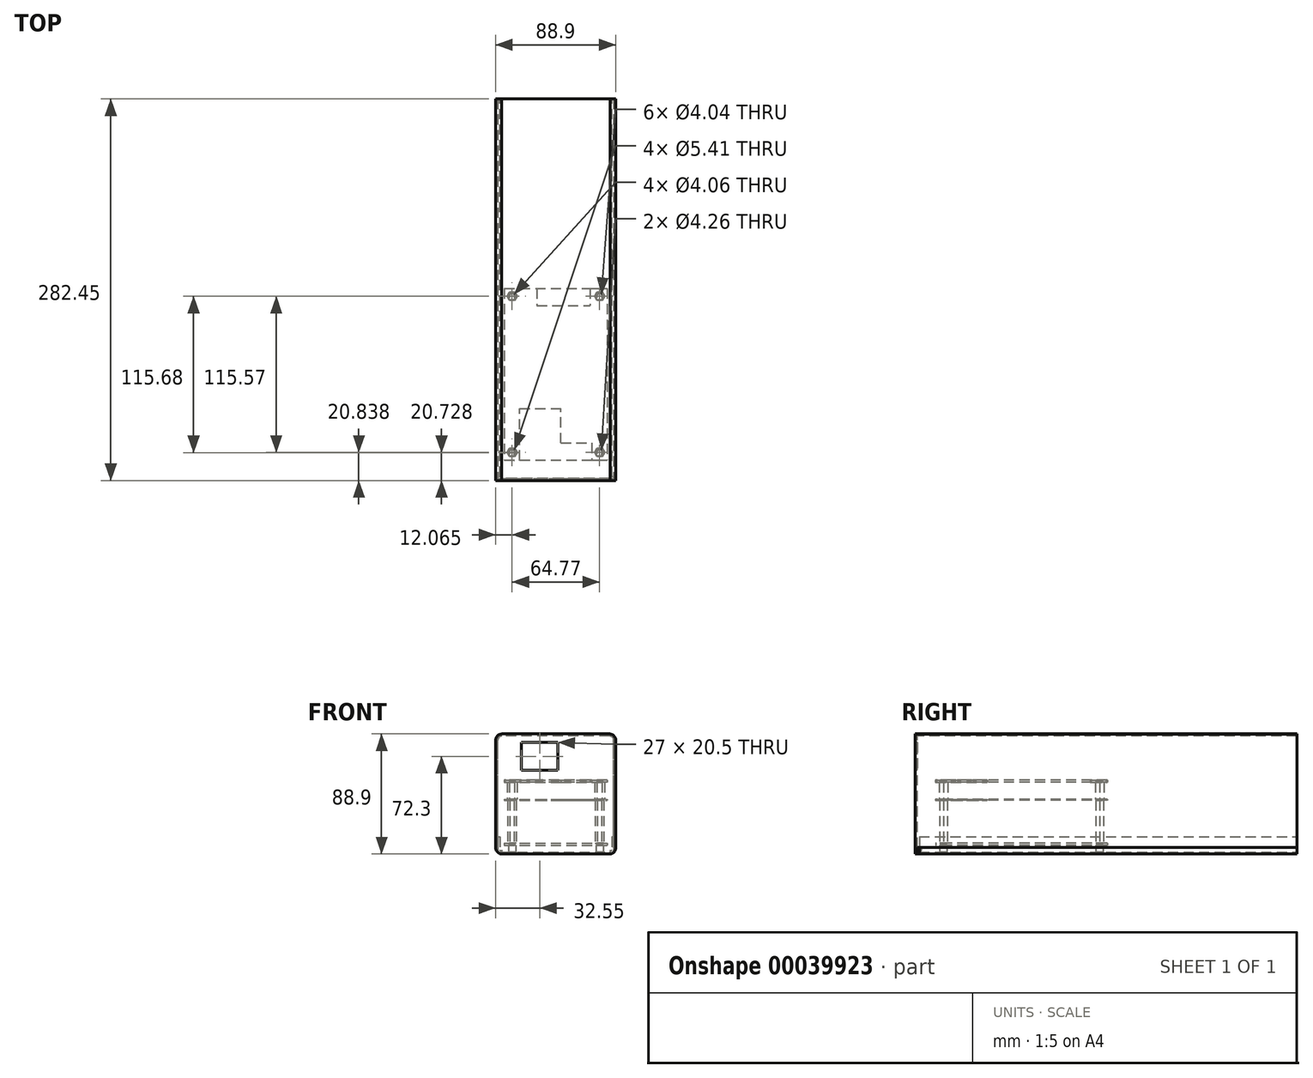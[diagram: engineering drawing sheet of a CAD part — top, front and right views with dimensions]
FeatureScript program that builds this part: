
annotation { "Feature Type Name" : "Feature", "Feature Type Description" : "" }
export const myFeature = defineFeature(function(context is Context, id is Id, definition is map)
    precondition{}
    {
        {
            var Q0;
            Q0=qCreatedBy(makeId("Front.planeOp"),FACE);
            var sketch = newSketch(context, id + "F0", { "sketchPlane" : qUnion([Q0])});
            skLineSegment(sketch, "E0.rect.top", {"start": v(-39.88, -44.45) * mm, "end": v(39.88, -44.45) * mm});
            skLineSegment(sketch, "E0.rect.left", {"start": v(-42.93, -31.75) * mm, "end": v(-42.93, -41.4) * mm});
            skLineSegment(sketch, "E0.rect.right", {"start": v(42.93, -31.75) * mm, "end": v(42.93, -41.4) * mm});
            skPoint(sketch, "E0.rect.middle", {"position": v(0, 0) * mm});
            skPoint(sketch, "E1.visualSharp", {"position": v(-42.93, 44.45) * mm});
            skPoint(sketch, "E2.visualSharp", {"position": v(42.93, 44.45) * mm});
            skPoint(sketch, "E3.visualSharp", {"position": v(42.93, -44.45) * mm});
            skArc(sketch, "E3.filletArc", {"start": v(39.88, -44.45) * mm, "mid": v(42.03, -43.56) * mm, "end": v(42.93, -41.4) * mm});
            skPoint(sketch, "E4.visualSharp", {"position": v(-42.93, -44.45) * mm});
            skArc(sketch, "E4.filletArc", {"start": v(-42.93, -41.4) * mm, "mid": v(-42.03, -43.56) * mm, "end": v(-39.88, -44.45) * mm});
            skLineSegment(sketch, "E5.3", {"start": v(41.4, -31.75) * mm, "end": v(41.4, -41.4) * mm});
            skLineSegment(sketch, "E5.4", {"start": v(-41.4, -31.75) * mm, "end": v(-41.4, -41.4) * mm});
            skLineSegment(sketch, "E6", {"start": v(-42.93, -31.75) * mm, "end": v(-41.4, -31.75) * mm});
            skLineSegment(sketch, "E7.trimOffspring", {"start": v(41.4, -31.75) * mm, "end": v(42.93, -31.75) * mm});
            skArc(sketch, "E8.0", {"start": v(39.88, -42.93) * mm, "mid": v(40.96, -42.48) * mm, "end": v(41.4, -41.4) * mm});
            skLineSegment(sketch, "E8.1", {"start": v(-39.88, -42.93) * mm, "end": v(39.88, -42.93) * mm});
            skArc(sketch, "E8.2", {"start": v(-41.4, -41.4) * mm, "mid": v(-40.96, -42.48) * mm, "end": v(-39.88, -42.93) * mm});
            skSolve(sketch);
        }
        {
            var Q0;
            Q0 = qSketchRegion(id + "F0", true);
            var Q1;
            Q1 = qConstructionFilter(qBodyType(qCreatedBy(id + "F0" ,EDGE), BodyType.WIRE), ConstructionObject.NO);
            extrude(context, id + "F1", {"entities" : qUnion([Q0]), "surfaceEntities" : qUnion([Q1]), "depth" : 152.4 * mm, "hasSecondDirection" : true, "secondDirectionOppositeDirection" : true, "secondDirectionDepth" : 127 * mm});
        }
        {
            var Q0;
            Q0=makeQuery(id+"F1.opExtrude","SWEPT_FACE",FACE,{"disambiguationData":[OSD([sQuery(id+"F0.wireOp",EDGE,"E8.1")])]});
            var sketch = newSketch(context, id + "F2", { "sketchPlane" : qUnion([Q0])});
            skLineSegment(sketch, "E9.rect.bottom", {"start": v(32.39, -19.04) * mm, "end": v(-32.39, -19.04) * mm, "construction": true});
            skLineSegment(sketch, "E9.rect.top", {"start": v(32.38, -134.61) * mm, "end": v(-32.39, -134.61) * mm, "construction": true});
            skLineSegment(sketch, "E9.rect.left", {"start": v(32.39, -19.04) * mm, "end": v(32.38, -134.61) * mm, "construction": true});
            skLineSegment(sketch, "E9.rect.right", {"start": v(-32.39, -19.04) * mm, "end": v(-32.39, -134.61) * mm, "construction": true});
            skPoint(sketch, "E9.rect.middle", {"position": v(0, -76.83) * mm});
            skCircle(sketch, "E10", {"center": v(-32.39, -19.04) * mm, "radius": 2.7 * mm});
            skCircle(sketch, "E11", {"center": v(32.39, -19.04) * mm, "radius": 2.7 * mm});
            skCircle(sketch, "E12", {"center": v(-32.39, -134.61) * mm, "radius": 2.7 * mm});
            skCircle(sketch, "E13", {"center": v(32.38, -134.61) * mm, "radius": 2.7 * mm});
            skSolve(sketch);
        }
        {
            var Q0;
            Q0 = qSketchRegion(id + "F2", true);
            extrude(context, id + "F3", {"entities" : qUnion([Q0]), "operationType" : NewBodyOperationType.REMOVE, "endBound" : BoundingType.THROUGH_ALL, "oppositeDirection" : true, "depth" : 25.4 * mm});
        }
        {
            var Q0;
            Q0=makeQuery(id+"F1.opExtrude","SWEPT_FACE",FACE,{"disambiguationData":[OSD([sQuery(id+"F0.wireOp",EDGE,"E8.1")])]});
            var sketch = newSketch(context, id + "F4", { "sketchPlane" : qUnion([Q0])});
            skCircle(sketch, "E14", {"center": v(-32.39, -19.04) * mm, "radius": 2.7 * mm});
            skCircle(sketch, "E15", {"center": v(32.39, -19.04) * mm, "radius": 2.7 * mm});
            skCircle(sketch, "E16", {"center": v(-32.39, -134.61) * mm, "radius": 2.7 * mm});
            skCircle(sketch, "E17", {"center": v(32.38, -134.61) * mm, "radius": 2.7 * mm});
            skSolve(sketch);
        }
        {
            var Q0;
            Q0 = qSketchRegion(id + "F4", true);
            extrude(context, id + "F5", {"entities" : qUnion([Q0]), "depth" : 4.83 * mm});
        }
        {
            var Q0;
            Q0=makeQuery(id+"F5.opExtrude","CAP_FACE",FACE,{"disambiguationData":[OSD([sQuery(id+"F4.wireOp",EDGE,"E14")])],"isStart":false});
            var sketch = newSketch(context, id + "F6", { "sketchPlane" : qUnion([Q0])});
            skLineSegment(sketch, "E18.rect.bottom", {"start": v(-38.1, -13.33) * mm, "end": v(38.1, -13.33) * mm});
            skLineSegment(sketch, "E18.rect.top", {"start": v(-38.1, -140.33) * mm, "end": v(38.1, -140.33) * mm});
            skLineSegment(sketch, "E18.rect.left", {"start": v(-38.1, -13.33) * mm, "end": v(-38.1, -140.33) * mm});
            skLineSegment(sketch, "E18.rect.right", {"start": v(38.1, -13.33) * mm, "end": v(38.1, -140.33) * mm});
            skPoint(sketch, "E18.rect.middle", {"position": v(0, -76.83) * mm});
            skLineSegment(sketch, "E19.rect.bottom", {"start": v(-32.39, -19.04) * mm, "end": v(32.39, -19.04) * mm, "construction": true});
            skLineSegment(sketch, "E19.rect.top", {"start": v(-32.39, -134.61) * mm, "end": v(32.39, -134.61) * mm, "construction": true});
            skLineSegment(sketch, "E19.rect.left", {"start": v(-32.39, -19.04) * mm, "end": v(-32.39, -134.61) * mm, "construction": true});
            skLineSegment(sketch, "E19.rect.right", {"start": v(32.39, -19.04) * mm, "end": v(32.39, -134.61) * mm, "construction": true});
            skCircle(sketch, "E20", {"center": v(-32.39, -19.04) * mm, "radius": 2.02 * mm});
            skCircle(sketch, "E21", {"center": v(32.39, -19.04) * mm, "radius": 2.02 * mm});
            skCircle(sketch, "E22", {"center": v(32.39, -134.61) * mm, "radius": 2.02 * mm});
            skCircle(sketch, "E23", {"center": v(-32.39, -134.61) * mm, "radius": 2.02 * mm});
            skSolve(sketch);
        }
        {
            var Q0;
            Q0 = qSketchRegion(id + "F6", true);
            extrude(context, id + "F7", {"entities" : qUnion([Q0]), "depth" : 1.6 * mm});
        }
        {
            var Q0;
            Q0=makeQuery(id+"F7.opExtrude","CAP_FACE",FACE,{"disambiguationData":[OSD([sQuery(id+"F6.wireOp",EDGE,"E18.rect.bottom"),sQuery(id+"F6.wireOp",EDGE,"E18.rect.top"),sQuery(id+"F6.wireOp",EDGE,"E18.rect.left"),sQuery(id+"F6.wireOp",EDGE,"E18.rect.right"),sQuery(id+"F6.wireOp",EDGE,"15a53e75-c34d-44fe-b530-c52fe133d88d.1"),sQuery(id+"F6.wireOp",EDGE,"E20"),sQuery(id+"F6.wireOp",EDGE,"E22"),sQuery(id+"F6.wireOp",EDGE,"E23")])],"isStart":false});
            var sketch = newSketch(context, id + "F8", { "sketchPlane" : qUnion([Q0])});
            skCircle(sketch, "E24.cCircle", {"center": v(-32.39, -19.04) * mm, "radius": 3.18 * mm, "construction": true});
            skLineSegment(sketch, "E24.0", {"start": v(-29.21, -19.04) * mm, "end": v(-30.8, -21.8) * mm});
            skLineSegment(sketch, "E24.1", {"start": v(-30.8, -21.8) * mm, "end": v(-33.97, -21.8) * mm});
            skLineSegment(sketch, "E24.2", {"start": v(-33.97, -21.8) * mm, "end": v(-35.56, -19.04) * mm});
            skLineSegment(sketch, "E24.3", {"start": v(-35.56, -19.04) * mm, "end": v(-33.97, -16.3) * mm});
            skLineSegment(sketch, "E24.4", {"start": v(-33.97, -16.3) * mm, "end": v(-30.8, -16.3) * mm});
            skLineSegment(sketch, "E24.5", {"start": v(-30.8, -16.3) * mm, "end": v(-29.21, -19.04) * mm});
            skCircle(sketch, "E25.cCircle", {"center": v(32.39, -19.04) * mm, "radius": 3.18 * mm, "construction": true});
            skLineSegment(sketch, "E25.0", {"start": v(29.21, -19.04) * mm, "end": v(30.8, -16.3) * mm});
            skLineSegment(sketch, "E25.1", {"start": v(30.8, -16.3) * mm, "end": v(33.97, -16.3) * mm});
            skLineSegment(sketch, "E25.2", {"start": v(33.97, -16.3) * mm, "end": v(35.56, -19.04) * mm});
            skLineSegment(sketch, "E25.3", {"start": v(35.56, -19.04) * mm, "end": v(33.97, -21.8) * mm});
            skLineSegment(sketch, "E25.4", {"start": v(33.97, -21.8) * mm, "end": v(30.8, -21.8) * mm});
            skLineSegment(sketch, "E25.5", {"start": v(30.8, -21.8) * mm, "end": v(29.21, -19.04) * mm});
            skCircle(sketch, "E26.cCircle", {"center": v(-32.39, -134.61) * mm, "radius": 3.18 * mm, "construction": true});
            skLineSegment(sketch, "E26.0", {"start": v(-29.2, -134.61) * mm, "end": v(-30.8, -137.36) * mm});
            skLineSegment(sketch, "E26.1", {"start": v(-30.8, -137.36) * mm, "end": v(-33.97, -137.36) * mm});
            skLineSegment(sketch, "E26.2", {"start": v(-33.97, -137.36) * mm, "end": v(-35.56, -134.61) * mm});
            skLineSegment(sketch, "E26.3", {"start": v(-35.56, -134.61) * mm, "end": v(-33.97, -131.86) * mm});
            skLineSegment(sketch, "E26.4", {"start": v(-33.97, -131.86) * mm, "end": v(-30.8, -131.86) * mm});
            skLineSegment(sketch, "E26.5", {"start": v(-30.8, -131.86) * mm, "end": v(-29.21, -134.61) * mm});
            skCircle(sketch, "E27.cCircle", {"center": v(32.39, -134.61) * mm, "radius": 3.18 * mm, "construction": true});
            skLineSegment(sketch, "E27.0", {"start": v(29.21, -134.61) * mm, "end": v(30.8, -131.86) * mm});
            skLineSegment(sketch, "E27.1", {"start": v(30.8, -131.86) * mm, "end": v(33.97, -131.86) * mm});
            skLineSegment(sketch, "E27.2", {"start": v(33.97, -131.86) * mm, "end": v(35.56, -134.61) * mm});
            skLineSegment(sketch, "E27.3", {"start": v(35.56, -134.61) * mm, "end": v(33.97, -137.36) * mm});
            skLineSegment(sketch, "E27.4", {"start": v(33.97, -137.36) * mm, "end": v(30.8, -137.36) * mm});
            skLineSegment(sketch, "E27.5", {"start": v(30.8, -137.36) * mm, "end": v(29.21, -134.61) * mm});
            skSolve(sketch);
        }
        {
            var Q0;
            Q0 = qSketchRegion(id + "F8", true);
            extrude(context, id + "F9", {"entities" : qUnion([Q0]), "depth" : 31.75 * mm});
        }
        {
            var Q0;
            Q0=makeQuery(id+"F9.opExtrude","CAP_FACE",FACE,{"disambiguationData":[OSD([sQuery(id+"F8.wireOp",EDGE,"E26.0"),sQuery(id+"F8.wireOp",EDGE,"E26.1"),sQuery(id+"F8.wireOp",EDGE,"E26.2"),sQuery(id+"F8.wireOp",EDGE,"E26.3"),sQuery(id+"F8.wireOp",EDGE,"E26.4"),sQuery(id+"F8.wireOp",EDGE,"E26.5")])],"isStart":false});
            var sketch = newSketch(context, id + "F10", { "sketchPlane" : qUnion([Q0])});
            skLineSegment(sketch, "E28.rect.bottom", {"start": v(-38.1, -13.33) * mm, "end": v(-13.97, -13.33) * mm});
            skLineSegment(sketch, "E28.rect.left", {"start": v(-38.1, -13.33) * mm, "end": v(-38.1, -102.23) * mm});
            skLineSegment(sketch, "E28.rect.right", {"start": v(38.1, -13.33) * mm, "end": v(38.1, -140.33) * mm});
            skPoint(sketch, "E28.rect.middle", {"position": v(0, -76.83) * mm});
            skCircle(sketch, "E29.0", {"center": v(-32.39, -19.04) * mm, "radius": 2.7 * mm, "construction": true});
            skCircle(sketch, "E29.1", {"center": v(32.39, -19.04) * mm, "radius": 2.7 * mm, "construction": true});
            skCircle(sketch, "E29.2", {"center": v(32.39, -134.61) * mm, "radius": 2.7 * mm, "construction": true});
            skCircle(sketch, "E29.3", {"center": v(-32.39, -134.61) * mm, "radius": 2.7 * mm, "construction": true});
            skCircle(sketch, "E30", {"center": v(-32.39, -19.04) * mm, "radius": 2.02 * mm});
            skCircle(sketch, "E31", {"center": v(32.39, -19.04) * mm, "radius": 2.02 * mm});
            skCircle(sketch, "E32", {"center": v(32.39, -134.61) * mm, "radius": 2.13 * mm});
            skLineSegment(sketch, "E33.top", {"start": v(-13.97, -26.03) * mm, "end": v(25.4, -26.03) * mm});
            skLineSegment(sketch, "E33.left", {"start": v(-13.97, -13.33) * mm, "end": v(-13.97, -26.03) * mm});
            skLineSegment(sketch, "E33.right", {"start": v(25.4, -13.33) * mm, "end": v(25.4, -26.03) * mm});
            skLineSegment(sketch, "E34.top", {"start": v(-26.67, -102.23) * mm, "end": v(3.8, -102.23) * mm});
            skLineSegment(sketch, "E34.right", {"start": v(3.81, -127.63) * mm, "end": v(3.8, -102.23) * mm});
            skLineSegment(sketch, "E35.bottom", {"start": v(3.81, -127.63) * mm, "end": v(26.67, -127.63) * mm});
            skLineSegment(sketch, "E35.right", {"start": v(26.67, -127.63) * mm, "end": v(26.67, -140.33) * mm});
            skPoint(sketch, "E36.orphan", {"position": v(-38.1, -140.33) * mm});
            skLineSegment(sketch, "E37", {"start": v(26.67, -140.33) * mm, "end": v(38.1, -140.33) * mm});
            skLineSegment(sketch, "E38.trimOffspring", {"start": v(25.4, -13.33) * mm, "end": v(38.1, -13.33) * mm});
            skLineSegment(sketch, "E39", {"start": v(-38.1, -102.23) * mm, "end": v(-38.1, -140.33) * mm});
            skLineSegment(sketch, "E40", {"start": v(-26.67, -140.55) * mm, "end": v(-26.67, -102.23) * mm});
            skLineSegment(sketch, "E41", {"start": v(-38.1, -140.33) * mm, "end": v(-26.67, -140.55) * mm});
            skCircle(sketch, "E42", {"center": v(-32.39, -134.61) * mm, "radius": 2.13 * mm});
            skSolve(sketch);
        }
        {
            var Q0;
            Q0 = qSketchRegion(id + "F10", true);
            extrude(context, id + "F11", {"entities" : qUnion([Q0]), "depth" : 0.74 * mm});
        }
        {
            var Q0;
            Q0=qCreatedBy(makeId("Right.planeOp"),FACE);
            var Q1;
            Q1=makeQuery(id+"F1.opExtrude","CAP_VERTEX",VERTEX,{"disambiguationData":[OSD([sQuery(id+"F0.wireOp",EDGE,"E8.1"),sQuery(id+"F0.wireOp",EDGE,"E8.2")])],"isStart":false});
            cPlane(context, id + "F12", {"entities" : qUnion([Q0, Q1]), "cplaneType" : CPlaneType.PLANE_POINT, "offset" : 152.4 * mm, "width" : 152.4 * mm, "height" : 152.4 * mm});
        }
        {
            var Q0;
            Q0=qCreatedBy(id+"F12.planeOp",FACE);
            var sketch = newSketch(context, id + "F13", { "sketchPlane" : qUnion([Q0])});
            skLineSegment(sketch, "E43", {"start": v(-153.92, -41.4) * mm, "end": v(-153.92, 44.45) * mm});
            skPoint(sketch, "E44.visualSharp", {"position": v(-153.92, -42.93) * mm});
            skArc(sketch, "E44.filletArc", {"start": v(-153.92, -41.4) * mm, "mid": v(-153.48, -42.48) * mm, "end": v(-152.4, -42.93) * mm});
            skLineSegment(sketch, "E45.0", {"start": v(-155.45, -41.4) * mm, "end": v(-155.45, 44.45) * mm});
            skArc(sketch, "E45.1", {"start": v(-155.45, -41.4) * mm, "mid": v(-154.56, -43.56) * mm, "end": v(-152.4, -44.45) * mm});
            skLineSegment(sketch, "E46", {"start": v(-153.92, 44.45) * mm, "end": v(-155.45, 44.45) * mm});
            skLineSegment(sketch, "E47", {"start": v(-152.4, -44.45) * mm, "end": v(-152.4, -42.93) * mm});
            skSolve(sketch);
        }
        {
            var Q0;
            Q0 = qSketchRegion(id + "F13", true);
            extrude(context, id + "F14", {"entities" : qUnion([Q0]), "operationType" : NewBodyOperationType.ADD, "depth" : 80.26 * mm});
        }
        {
            var Q0;
            Q0=makeQuery(id+"F14.opExtrude","SWEPT_FACE",FACE,{"disambiguationData":[OSD([sQuery(id+"F13.wireOp",EDGE,"E45.0")])]});
            var sketch = newSketch(context, id + "F15", { "sketchPlane" : qUnion([Q0])});
            skLineSegment(sketch, "E48.rect.bottom", {"start": v(-39.69, 44.45) * mm, "end": v(39.69, 44.45) * mm});
            skLineSegment(sketch, "E48.rect.top", {"start": v(-39.69, -44.45) * mm, "end": v(39.69, -44.45) * mm});
            skLineSegment(sketch, "E48.rect.left", {"start": v(-44.45, 39.69) * mm, "end": v(-44.45, -39.69) * mm});
            skLineSegment(sketch, "E48.rect.right", {"start": v(44.45, 39.69) * mm, "end": v(44.45, -39.69) * mm});
            skPoint(sketch, "E48.rect.middle", {"position": v(0, 0) * mm});
            skPoint(sketch, "E49.visualSharp", {"position": v(-44.45, 44.45) * mm});
            skArc(sketch, "E49.filletArc", {"start": v(-39.69, 44.45) * mm, "mid": v(-43.06, 43.06) * mm, "end": v(-44.45, 39.69) * mm});
            skPoint(sketch, "E50.visualSharp", {"position": v(44.45, 44.45) * mm});
            skArc(sketch, "E50.filletArc", {"start": v(44.45, 39.69) * mm, "mid": v(43.06, 43.06) * mm, "end": v(39.69, 44.45) * mm});
            skPoint(sketch, "E51.visualSharp", {"position": v(44.45, -44.45) * mm});
            skArc(sketch, "E51.filletArc", {"start": v(39.69, -44.45) * mm, "mid": v(43.06, -43.06) * mm, "end": v(44.45, -39.69) * mm});
            skPoint(sketch, "E52.visualSharp", {"position": v(-44.45, -44.45) * mm});
            skArc(sketch, "E52.filletArc", {"start": v(-44.45, -39.69) * mm, "mid": v(-43.06, -43.06) * mm, "end": v(-39.69, -44.45) * mm});
            skSolve(sketch);
        }
        {
            var Q0;
            Q0 = qSketchRegion(id + "F15", true);
            extrude(context, id + "F16", {"entities" : qUnion([Q0]), "operationType" : NewBodyOperationType.ADD, "oppositeDirection" : true, "depth" : 1.52 * mm});
        }
        {
            var Q0;
            Q0=makeQuery(id+"F16.boolean.opBoolean","MERGE",FACE,{"derivedFrom":[makeQuery(id+"F14.opExtrude","SWEPT_FACE",FACE,{"disambiguationData":[OSD([sQuery(id+"F13.wireOp",EDGE,"E45.0")])]}),makeQuery(id+"F16.opExtrude","CAP_FACE",FACE,{"disambiguationData":[OSD([sQuery(id+"F15.wireOp",EDGE,"E48.rect.bottom"),sQuery(id+"F15.wireOp",EDGE,"E48.rect.top"),sQuery(id+"F15.wireOp",EDGE,"E48.rect.left"),sQuery(id+"F15.wireOp",EDGE,"E48.rect.right"),sQuery(id+"F15.wireOp",EDGE,"E49.filletArc"),sQuery(id+"F15.wireOp",EDGE,"E50.filletArc"),sQuery(id+"F15.wireOp",EDGE,"E51.filletArc"),sQuery(id+"F15.wireOp",EDGE,"E52.filletArc")])],"isStart":true})]});
            var sketch = newSketch(context, id + "F17", { "sketchPlane" : qUnion([Q0])});
            skLineSegment(sketch, "E53.rect.bottom", {"start": v(-25.4, 38.1) * mm, "end": v(1.6, 38.1) * mm});
            skLineSegment(sketch, "E53.rect.top", {"start": v(-25.4, 17.6) * mm, "end": v(1.6, 17.6) * mm});
            skLineSegment(sketch, "E53.rect.left", {"start": v(-25.4, 38.1) * mm, "end": v(-25.4, 17.6) * mm});
            skLineSegment(sketch, "E53.rect.right", {"start": v(1.6, 38.1) * mm, "end": v(1.6, 17.6) * mm});
            skPoint(sketch, "E53.rect.middle", {"position": v(-11.9, 27.85) * mm});
            skSolve(sketch);
        }
        {
            var Q0;
            Q0 = qSketchRegion(id + "F17", true);
            extrude(context, id + "F18", {"entities" : qUnion([Q0]), "operationType" : NewBodyOperationType.REMOVE, "oppositeDirection" : true, "depth" : 25.4 * mm});
        }
        {
            var Q0;
            Q0=makeQuery(id+"F11.opExtrude","CAP_FACE",FACE,{"disambiguationData":[OSD([sQuery(id+"F10.wireOp",EDGE,"E28.rect.bottom"),sQuery(id+"F10.wireOp",EDGE,"E28.rect.left"),sQuery(id+"F10.wireOp",EDGE,"E28.rect.right"),sQuery(id+"F10.wireOp",EDGE,"E30"),sQuery(id+"F10.wireOp",EDGE,"E31"),sQuery(id+"F10.wireOp",EDGE,"E32"),sQuery(id+"F10.wireOp",EDGE,"E33.top"),sQuery(id+"F10.wireOp",EDGE,"E33.left"),sQuery(id+"F10.wireOp",EDGE,"E33.right"),sQuery(id+"F10.wireOp",EDGE,"E34.top"),sQuery(id+"F10.wireOp",EDGE,"E34.right"),sQuery(id+"F10.wireOp",EDGE,"E35.bottom"),sQuery(id+"F10.wireOp",EDGE,"E35.right"),sQuery(id+"F10.wireOp",EDGE,"E37"),sQuery(id+"F10.wireOp",EDGE,"E38.trimOffspring"),sQuery(id+"F10.wireOp",EDGE,"E39"),sQuery(id+"F10.wireOp",EDGE,"E40"),sQuery(id+"F10.wireOp",EDGE,"E41"),sQuery(id+"F10.wireOp",EDGE,"E42")])],"isStart":false});
            var sketch = newSketch(context, id + "F19", { "sketchPlane" : qUnion([Q0])});
            skCircle(sketch, "E54.cCircle", {"center": v(-32.39, -19.04) * mm, "radius": 3.67 * mm, "construction": true});
            skLineSegment(sketch, "E54.0", {"start": v(-28.72, -19.04) * mm, "end": v(-30.55, -22.22) * mm});
            skLineSegment(sketch, "E54.1", {"start": v(-30.55, -22.22) * mm, "end": v(-34.22, -22.22) * mm});
            skLineSegment(sketch, "E54.2", {"start": v(-34.22, -22.22) * mm, "end": v(-36.05, -19.04) * mm});
            skLineSegment(sketch, "E54.3", {"start": v(-36.05, -19.04) * mm, "end": v(-34.22, -15.87) * mm});
            skLineSegment(sketch, "E54.4", {"start": v(-34.22, -15.87) * mm, "end": v(-30.55, -15.87) * mm});
            skLineSegment(sketch, "E54.5", {"start": v(-30.55, -15.87) * mm, "end": v(-28.72, -19.04) * mm});
            skCircle(sketch, "E55.cCircle", {"center": v(32.39, -19.04) * mm, "radius": 3.67 * mm, "construction": true});
            skLineSegment(sketch, "E55.0", {"start": v(28.72, -19.04) * mm, "end": v(30.55, -15.87) * mm});
            skLineSegment(sketch, "E55.1", {"start": v(30.55, -15.87) * mm, "end": v(34.22, -15.87) * mm});
            skLineSegment(sketch, "E55.2", {"start": v(34.22, -15.87) * mm, "end": v(36.05, -19.04) * mm});
            skLineSegment(sketch, "E55.3", {"start": v(36.05, -19.04) * mm, "end": v(34.22, -22.22) * mm});
            skLineSegment(sketch, "E55.4", {"start": v(34.22, -22.22) * mm, "end": v(30.55, -22.22) * mm});
            skLineSegment(sketch, "E55.5", {"start": v(30.55, -22.22) * mm, "end": v(28.72, -19.04) * mm});
            skCircle(sketch, "E56.cCircle", {"center": v(-32.39, -134.61) * mm, "radius": 3.67 * mm, "construction": true});
            skLineSegment(sketch, "E56.0", {"start": v(-28.72, -134.61) * mm, "end": v(-30.55, -137.79) * mm});
            skLineSegment(sketch, "E56.1", {"start": v(-30.55, -137.79) * mm, "end": v(-34.22, -137.79) * mm});
            skLineSegment(sketch, "E56.2", {"start": v(-34.22, -137.79) * mm, "end": v(-36.05, -134.61) * mm});
            skLineSegment(sketch, "E56.3", {"start": v(-36.05, -134.61) * mm, "end": v(-34.22, -131.44) * mm});
            skLineSegment(sketch, "E56.4", {"start": v(-34.22, -131.44) * mm, "end": v(-30.55, -131.44) * mm});
            skLineSegment(sketch, "E56.5", {"start": v(-30.55, -131.44) * mm, "end": v(-28.72, -134.61) * mm});
            skCircle(sketch, "E57.cCircle", {"center": v(32.39, -134.61) * mm, "radius": 3.67 * mm, "construction": true});
            skLineSegment(sketch, "E57.0", {"start": v(28.72, -134.61) * mm, "end": v(30.55, -131.44) * mm});
            skLineSegment(sketch, "E57.1", {"start": v(30.55, -131.44) * mm, "end": v(34.22, -131.44) * mm});
            skLineSegment(sketch, "E57.2", {"start": v(34.22, -131.44) * mm, "end": v(36.05, -134.61) * mm});
            skLineSegment(sketch, "E57.3", {"start": v(36.05, -134.61) * mm, "end": v(34.22, -137.79) * mm});
            skLineSegment(sketch, "E57.4", {"start": v(34.22, -137.79) * mm, "end": v(30.55, -137.79) * mm});
            skLineSegment(sketch, "E57.5", {"start": v(30.55, -137.79) * mm, "end": v(28.72, -134.61) * mm});
            skSolve(sketch);
        }
        {
            var Q0;
            Q0 = qSketchRegion(id + "F19", true);
            extrude(context, id + "F20", {"entities" : qUnion([Q0]), "depth" : 12.7 * mm});
        }
        {
            var Q0;
            Q0=makeQuery(id+"F20.opExtrude","CAP_FACE",FACE,{"disambiguationData":[OSD([sQuery(id+"F19.wireOp",EDGE,"E55.0"),sQuery(id+"F19.wireOp",EDGE,"E55.1"),sQuery(id+"F19.wireOp",EDGE,"E55.2"),sQuery(id+"F19.wireOp",EDGE,"E55.3"),sQuery(id+"F19.wireOp",EDGE,"E55.4"),sQuery(id+"F19.wireOp",EDGE,"E55.5")])],"isStart":false});
            var sketch = newSketch(context, id + "F21", { "sketchPlane" : qUnion([Q0])});
            skLineSegment(sketch, "E58.0.0", {"start": v(-13.97, -13.33) * mm, "end": v(-38.1, -13.33) * mm});
            skLineSegment(sketch, "E58.0.1", {"start": v(-38.1, -13.33) * mm, "end": v(-38.1, -140.33) * mm});
            skLineSegment(sketch, "E58.0.2", {"start": v(-38.1, -140.33) * mm, "end": v(-26.67, -140.55) * mm});
            skLineSegment(sketch, "E58.0.3", {"start": v(-26.67, -140.55) * mm, "end": v(-26.67, -102.23) * mm});
            skLineSegment(sketch, "E58.0.4", {"start": v(-26.67, -102.23) * mm, "end": v(3.8, -102.23) * mm});
            skLineSegment(sketch, "E58.0.5", {"start": v(3.8, -102.23) * mm, "end": v(3.81, -127.63) * mm});
            skLineSegment(sketch, "E58.0.6", {"start": v(3.81, -127.63) * mm, "end": v(26.67, -127.63) * mm});
            skLineSegment(sketch, "E58.0.7", {"start": v(26.67, -127.63) * mm, "end": v(26.67, -140.33) * mm});
            skLineSegment(sketch, "E58.0.8", {"start": v(26.67, -140.33) * mm, "end": v(38.1, -140.33) * mm});
            skLineSegment(sketch, "E58.0.9", {"start": v(38.1, -140.33) * mm, "end": v(38.1, -13.33) * mm});
            skLineSegment(sketch, "E58.0.10", {"start": v(38.1, -13.33) * mm, "end": v(25.4, -13.33) * mm});
            skLineSegment(sketch, "E58.0.11", {"start": v(25.4, -13.33) * mm, "end": v(25.4, -26.03) * mm});
            skLineSegment(sketch, "E58.0.12", {"start": v(25.4, -26.03) * mm, "end": v(-13.97, -26.03) * mm});
            skLineSegment(sketch, "E58.0.13", {"start": v(-13.97, -26.03) * mm, "end": v(-13.97, -13.33) * mm});
            skCircle(sketch, "E59", {"center": v(-32.39, -19.04) * mm, "radius": 2.03 * mm});
            skCircle(sketch, "E60", {"center": v(32.39, -19.04) * mm, "radius": 2.03 * mm});
            skCircle(sketch, "E61", {"center": v(-32.39, -134.72) * mm, "radius": 2.03 * mm});
            skCircle(sketch, "E62", {"center": v(32.38, -134.61) * mm, "radius": 2.03 * mm});
            skSolve(sketch);
        }
        {
            var Q0;
            Q0 = qSketchRegion(id + "F21", true);
            extrude(context, id + "F22", {"entities" : qUnion([Q0]), "depth" : 1.6 * mm});
        }
        {
            var Q0;
            Q0=makeQuery(id+"F16.boolean.opBoolean","MERGE",FACE,{"derivedFrom":[makeQuery(id+"F14.opExtrude","SWEPT_FACE",FACE,{"disambiguationData":[OSD([sQuery(id+"F13.wireOp",EDGE,"E43")])]}),makeQuery(id+"F16.opExtrude","CAP_FACE",FACE,{"disambiguationData":[OSD([sQuery(id+"F15.wireOp",EDGE,"E48.rect.bottom"),sQuery(id+"F15.wireOp",EDGE,"E48.rect.top"),sQuery(id+"F15.wireOp",EDGE,"E48.rect.left"),sQuery(id+"F15.wireOp",EDGE,"E48.rect.right"),sQuery(id+"F15.wireOp",EDGE,"E49.filletArc"),sQuery(id+"F15.wireOp",EDGE,"E50.filletArc"),sQuery(id+"F15.wireOp",EDGE,"E51.filletArc"),sQuery(id+"F15.wireOp",EDGE,"E52.filletArc")])],"isStart":false})]});
            var sketch = newSketch(context, id + "F23", { "sketchPlane" : qUnion([Q0])});
            skArc(sketch, "E63.1", {"start": v(-44.45, 39.69) * mm, "mid": v(-43.3, 42.8) * mm, "end": v(-40.39, 44.4) * mm});
            skLineSegment(sketch, "E63.3", {"start": v(44.45, 39.69) * mm, "end": v(44.45, 39.69) * mm});
            skLineSegment(sketch, "E64", {"start": v(-44.45, -39.69) * mm, "end": v(-44.45, 39.69) * mm});
            skLineSegment(sketch, "E65", {"start": v(44.45, -39.69) * mm, "end": v(44.45, 39.69) * mm});
            skLineSegment(sketch, "E66", {"start": v(39.88, 44.45) * mm, "end": v(-40.39, 44.45) * mm});
            skArc(sketch, "E67.0", {"start": v(39.57, 42.92) * mm, "mid": v(41.94, 42.02) * mm, "end": v(42.93, 39.69) * mm});
            skLineSegment(sketch, "E67.1", {"start": v(42.93, -39.69) * mm, "end": v(42.93, 39.69) * mm});
            skArc(sketch, "E68.0", {"start": v(-42.93, 39.69) * mm, "mid": v(-41.98, 41.97) * mm, "end": v(-39.7, 42.93) * mm});
            skLineSegment(sketch, "E68.1", {"start": v(-42.93, -39.69) * mm, "end": v(-42.93, 39.69) * mm});
            skLineSegment(sketch, "E69", {"start": v(-39.7, 42.93) * mm, "end": v(39.57, 42.92) * mm});
            skLineSegment(sketch, "E70", {"start": v(-42.93, -39.69) * mm, "end": v(-44.45, -39.69) * mm});
            skLineSegment(sketch, "E71", {"start": v(42.93, -39.69) * mm, "end": v(44.45, -39.69) * mm});
            skSolve(sketch);
        }
        {
            var Q0;
            Q0=makeQuery(id+"F23.imprint","IMPRINT",FACE,{"disambiguationData":[TD([[makeQuery(id+"F23.imprint","IMPRINT",EDGE,{"derivedFrom":sQuery(id+"F23.wireOp",EDGE,"E63.1")}),-1.0]])]});
            extrude(context, id + "F24", {"entities" : qUnion([Q0]), "operationType" : NewBodyOperationType.ADD, "depth" : 280.92 * mm});
        }
    });
